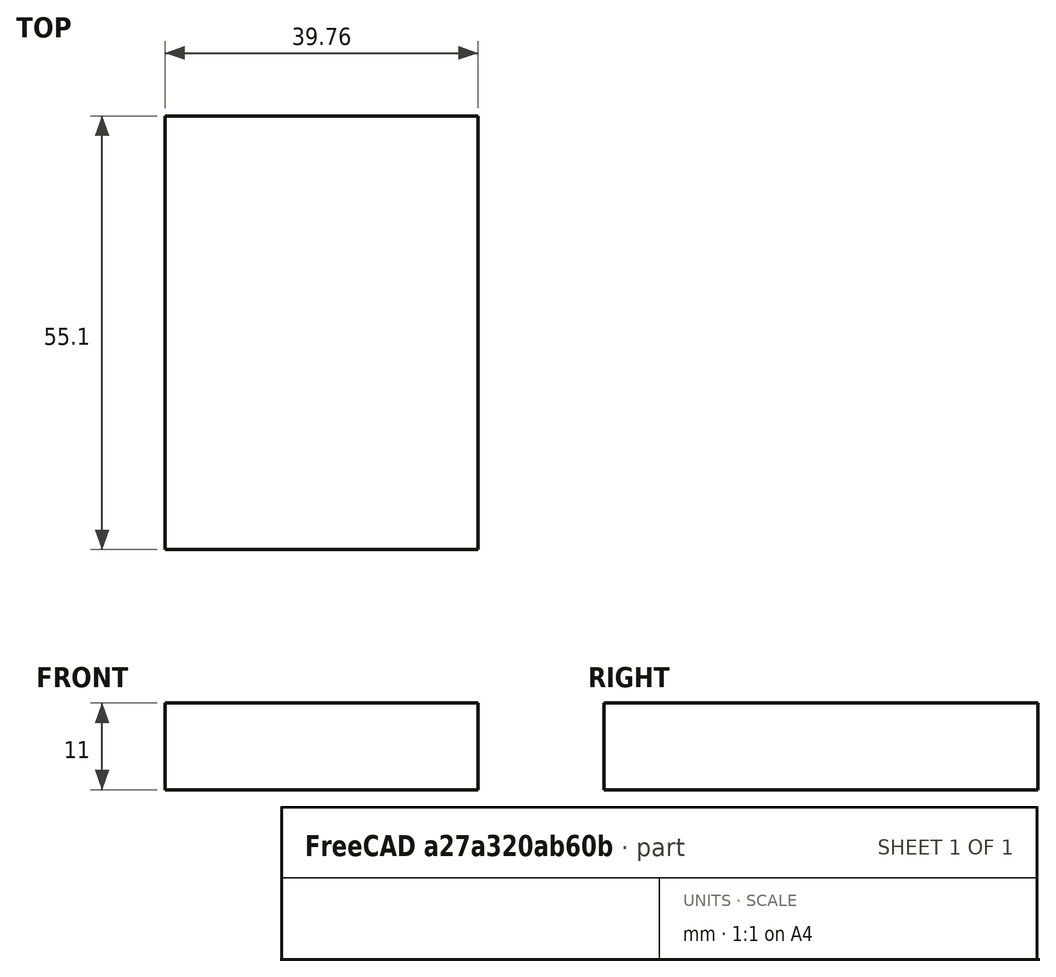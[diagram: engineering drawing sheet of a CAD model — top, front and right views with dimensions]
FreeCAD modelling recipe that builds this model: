
FCSTD DOCUMENT  (FreeCAD 0.20R29410 (Git))
Label: electronics
License: All rights reserved
LicenseURL: http://en.wikipedia.org/wiki/All_rights_reserved
objects: Sketcher::SketchObject×1, PartDesign::Pad×1, PartDesign::Body×1, App::Link×1
note: 4 computed .brp shape members not serialized (recipe doc carries the construction recipe); baked Part::Feature solids carry a one-line shape summary decoded from their .brp

FEATURE [Sketcher::SketchObject] Sketch
  FullyConstrained = true
  MapMode = 5
  Support = -> [XY_Plane]
  sketch-geometry (4):
    g0: LineSegment StartX=-19.875 StartY=27.55 StartZ=0 EndX=19.875 EndY=27.55 EndZ=0
    g1: LineSegment StartX=19.875 StartY=27.55 StartZ=0 EndX=19.875 EndY=-27.55 EndZ=0
    g2: LineSegment StartX=19.875 StartY=-27.55 StartZ=0 EndX=-19.875 EndY=-27.55 EndZ=0
    g3: LineSegment StartX=-19.875 StartY=-27.55 StartZ=0 EndX=-19.875 EndY=27.55 EndZ=0
  constraints (10):
    c: Coincident(g0,g1)
    c: Coincident(g1,g2)
    c: Coincident(g2,g3)
    c: Coincident(g3,g0)
    c: Horizontal(g2)
    c: Vertical(g1)
    c: DistanceY(g1,g1) = 55.1
    c: DistanceX(g0,g0) = 39.75
    c: Symmetric(g0,g0,g-2)
    c: Symmetric(g2,g0,g-1)
FEATURE [PartDesign::Pad] Pad  label="pad"
  Direction = (0,0,1)
  Length = 11
  Length2 = 10
  Profile = -> Sketch
  ReferenceAxis = -> Sketch [N_Axis]
  Type = 0
FEATURE [PartDesign::Body] Body  label="electronics"
  Group = -> [Sketch,Pad]
  Origin = -> Origin
  Tip = -> Pad
FEATURE [App::Link] Link  label="electronics001"
  LinkedObject = -> Body
